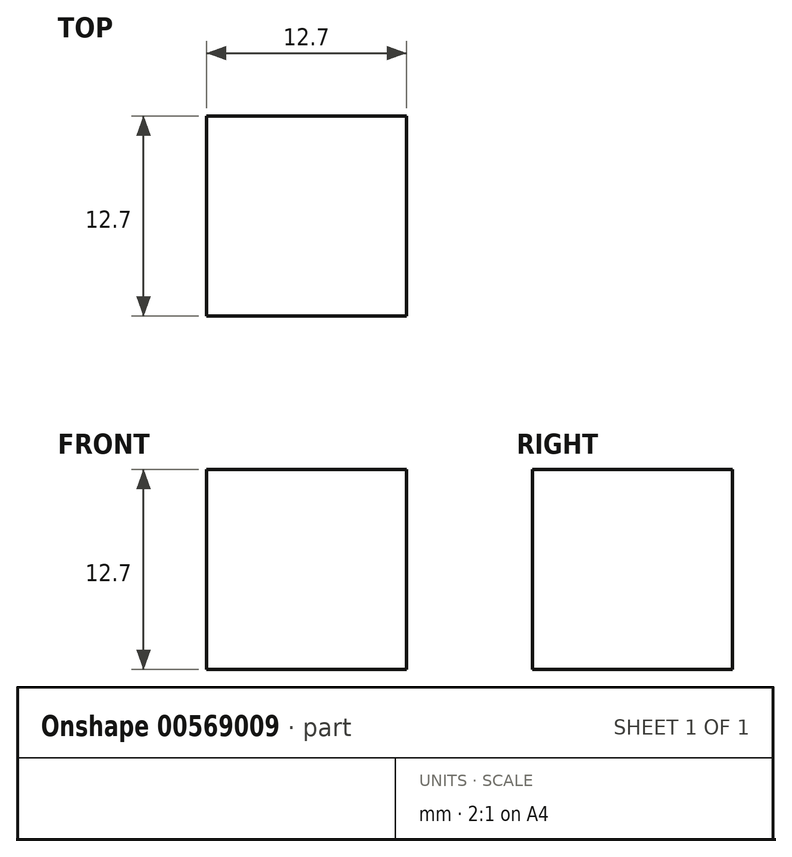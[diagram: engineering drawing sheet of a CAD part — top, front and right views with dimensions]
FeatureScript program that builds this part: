
annotation { "Feature Type Name" : "Feature", "Feature Type Description" : "" }
export const myFeature = defineFeature(function(context is Context, id is Id, definition is map)
    precondition{}
    {
        {
            var Q0;
            Q0=qCreatedBy(makeId("Front.planeOp"),FACE);
            var sketch = newSketch(context, id + "F0", { "sketchPlane" : qUnion([Q0])});
            skLineSegment(sketch, "E0.bottom", {"start": v(0, 0) * mm, "end": v(12.7, 0) * mm});
            skLineSegment(sketch, "E0.top", {"start": v(0, 12.7) * mm, "end": v(12.7, 12.7) * mm});
            skLineSegment(sketch, "E0.left", {"start": v(0, 0) * mm, "end": v(0, 12.7) * mm});
            skLineSegment(sketch, "E0.right", {"start": v(12.7, 0) * mm, "end": v(12.7, 12.7) * mm});
            skSolve(sketch);
        }
        {
            var Q0;
            Q0=makeQuery(id+"F0.imprint","IMPRINT",FACE,{"disambiguationData":[TD([[makeQuery(id+"F0.imprint","IMPRINT",EDGE,{"derivedFrom":sQuery(id+"F0.wireOp",EDGE,"E0.bottom")}),1.0]])]});
            extrude(context, id + "F1", {"entities" : qUnion([Q0]), "depth" : 12.7 * mm, "offsetDistance" : 25.4 * mm});
        }
    });
